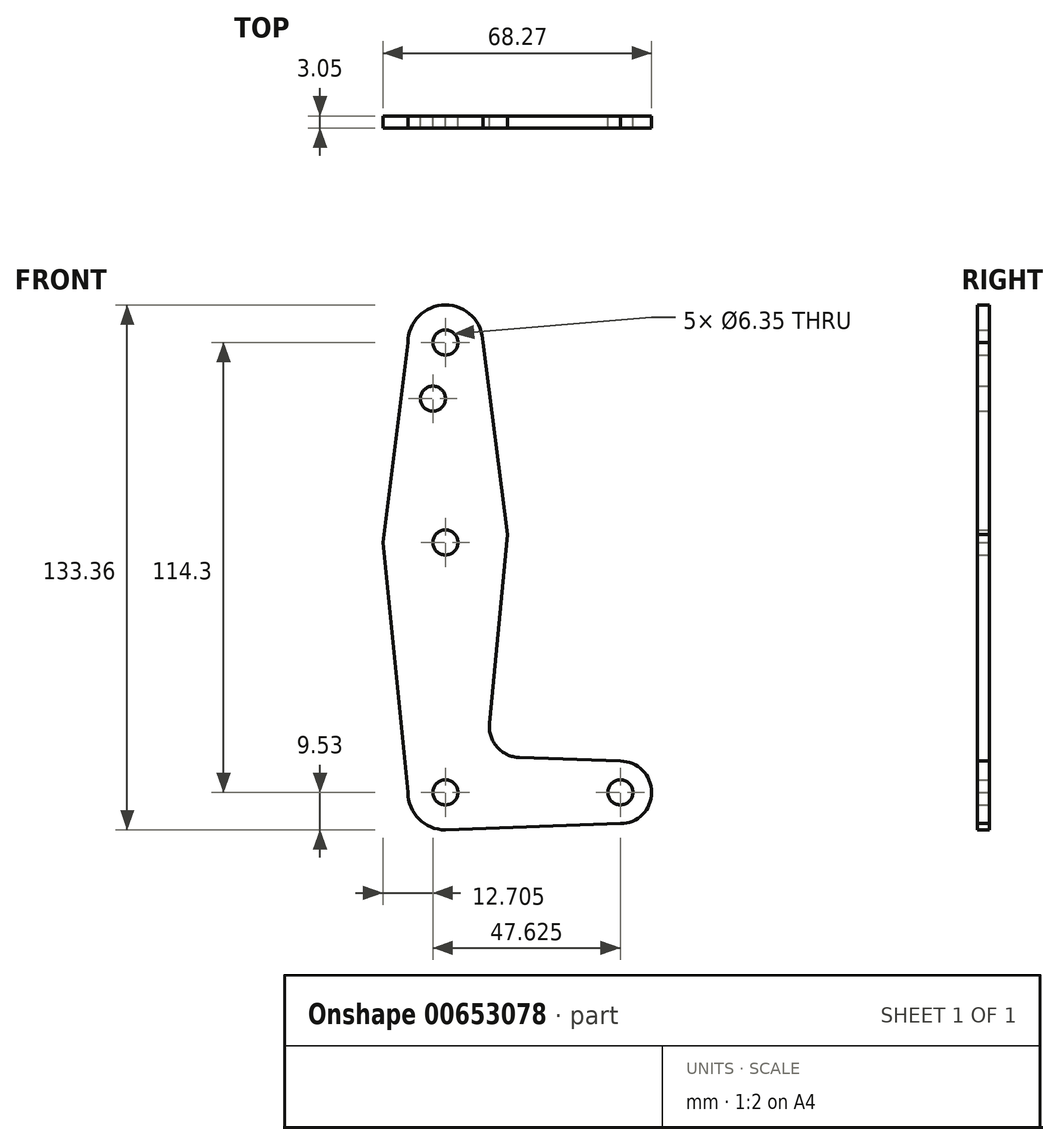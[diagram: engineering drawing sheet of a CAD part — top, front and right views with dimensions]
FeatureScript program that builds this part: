
annotation { "Feature Type Name" : "Feature", "Feature Type Description" : "" }
export const myFeature = defineFeature(function(context is Context, id is Id, definition is map)
    precondition{}
    {
        {
            var Q0;
            Q0=qCreatedBy(makeId("Front.planeOp"),FACE);
            var sketch = newSketch(context, id + "F0", { "sketchPlane" : qUnion([Q0])});
            skLineSegment(sketch, "E0", {"start": v(0, 0) * mm, "end": v(0, 114.3) * mm});
            skLineSegment(sketch, "E1", {"start": v(0, 0) * mm, "end": v(44.45, 0) * mm});
            skCircle(sketch, "E2", {"center": v(0, 114.3) * mm, "radius": 9.53 * mm});
            skCircle(sketch, "E3", {"center": v(0, 0) * mm, "radius": 9.53 * mm});
            skCircle(sketch, "E4", {"center": v(44.45, 0) * mm, "radius": 7.94 * mm});
            skCircle(sketch, "E5", {"center": v(0, 63.5) * mm, "radius": 15.88 * mm});
            skLineSegment(sketch, "E6", {"start": v(-9.52, 114.3) * mm, "end": v(-15.88, 63.5) * mm});
            skLineSegment(sketch, "E7", {"start": v(-15.87, 63.5) * mm, "end": v(-9.53, 0) * mm});
            skLineSegment(sketch, "E8", {"start": v(9.53, 114.3) * mm, "end": v(15.75, 65.5) * mm});
            skLineSegment(sketch, "E9", {"start": v(15.75, 65.5) * mm, "end": v(11.2, 17.55) * mm});
            skLineSegment(sketch, "E10", {"start": v(0, -9.52) * mm, "end": v(44.45, -7.94) * mm});
            skLineSegment(sketch, "E11", {"start": v(18.82, 8.85) * mm, "end": v(44.45, 7.94) * mm});
            skCircle(sketch, "E12", {"center": v(0, 114.3) * mm, "radius": 3.18 * mm});
            skCircle(sketch, "E13", {"center": v(0, 63.5) * mm, "radius": 3.18 * mm});
            skCircle(sketch, "E14", {"center": v(0, 0) * mm, "radius": 3.18 * mm});
            skCircle(sketch, "E15", {"center": v(44.45, 0) * mm, "radius": 3.18 * mm});
            skCircle(sketch, "E16", {"center": v(-3.18, 100.03) * mm, "radius": 3.18 * mm});
            skArc(sketch, "E17.filletArc", {"start": v(11.2, 17.55) * mm, "mid": v(13.13, 11.55) * mm, "end": v(18.82, 8.85) * mm});
            skSolve(sketch);
        }
        {
            var Q0;
            Q0=makeQuery(id+"F0.imprint","IMPRINT",FACE,{"disambiguationData":[TD([[makeQuery(id+"F0.imprint","IMPRINT",EDGE,{"derivedFrom":sQuery(id+"F0.wireOp",EDGE,"E12")}),-1.0]])]});
            var Q1;
            {var subQ0=sQuery(id+"F0.wireOp",EDGE,"E8");Q1=makeQuery(id+"F0.imprint","IMPRINT",FACE,{"disambiguationData":[TD([[makeQuery(id+"F0.imprint","IMPRINT",EDGE,{"derivedFrom":subQ0}),-1.0]])]});}
            var Q2;
            {var subQ8=sQuery(id+"F0.wireOp",EDGE,"E16");Q2=makeQuery(id+"F0.imprint","IMPRINT",FACE,{"disambiguationData":[TD([[makeQuery(id+"F0.imprint","IMPRINT",EDGE,{"derivedFrom":subQ8}),-1.0]])]});}
            var Q3;
            {var subQ1=sQuery(id+"F0.wireOp",EDGE,"E5");var subQ3=sQuery(id+"F0.wireOp",EDGE,"E0");var subQ4=makeQuery(id+"F0.imprint","INTERSECT",VERTEX,{"disambiguationData":[OD(0.0)],"derivedFrom":[subQ3,subQ1]});Q3=makeQuery(id+"F0.imprint","IMPRINT",FACE,{"disambiguationData":[TD([[makeQuery(id+"F0.imprint","IMPRINT",EDGE,{"disambiguationData":[TD([[subQ4,-1.0]])],"derivedFrom":subQ3}),1.0]])]});}
            var Q4;
            {var subQ1=sQuery(id+"F0.wireOp",EDGE,"E5");var subQ3=sQuery(id+"F0.wireOp",EDGE,"E0");var subQ4=makeQuery(id+"F0.imprint","INTERSECT",VERTEX,{"disambiguationData":[OD(0.0)],"derivedFrom":[subQ3,subQ1]});Q4=makeQuery(id+"F0.imprint","IMPRINT",FACE,{"disambiguationData":[TD([[makeQuery(id+"F0.imprint","IMPRINT",EDGE,{"disambiguationData":[TD([[subQ4,-1.0]])],"derivedFrom":subQ3}),-1.0]])]});}
            var Q5;
            {var subQ0=sQuery(id+"F0.wireOp",EDGE,"E11");Q5=makeQuery(id+"F0.imprint","IMPRINT",FACE,{"disambiguationData":[TD([[makeQuery(id+"F0.imprint","IMPRINT",EDGE,{"derivedFrom":subQ0}),-1.0]])]});}
            var Q6;
            {var subQ0=sQuery(id+"F0.wireOp",EDGE,"E3");var subQ1=sQuery(id+"F0.wireOp",EDGE,"E0");var subQ2=makeQuery(id+"F0.imprint","INTERSECT",VERTEX,{"derivedFrom":[subQ1,subQ0]});Q6=makeQuery(id+"F0.imprint","IMPRINT",FACE,{"disambiguationData":[TD([[makeQuery(id+"F0.imprint","IMPRINT",EDGE,{"disambiguationData":[TD([[subQ2,-1.0]])],"derivedFrom":subQ1}),1.0]])]});}
            var Q7;
            {var subQ0=sQuery(id+"F0.wireOp",EDGE,"E14");var subQ1=sQuery(id+"F0.wireOp",EDGE,"E0");var subQ2=makeQuery(id+"F0.imprint","INTERSECT",VERTEX,{"derivedFrom":[subQ1,subQ0]});Q7=makeQuery(id+"F0.imprint","IMPRINT",FACE,{"disambiguationData":[TD([[makeQuery(id+"F0.imprint","IMPRINT",EDGE,{"disambiguationData":[TD([[subQ2,-1.0]])],"derivedFrom":subQ1}),-1.0]])]});}
            var Q8;
            {var subQ0=sQuery(id+"F0.wireOp",EDGE,"E4");var subQ1=sQuery(id+"F0.wireOp",EDGE,"E1");var subQ2=makeQuery(id+"F0.imprint","INTERSECT",VERTEX,{"derivedFrom":[subQ1,subQ0]});Q8=makeQuery(id+"F0.imprint","IMPRINT",FACE,{"disambiguationData":[TD([[makeQuery(id+"F0.imprint","IMPRINT",EDGE,{"disambiguationData":[TD([[subQ2,1.0]])],"derivedFrom":subQ1}),-1.0]])]});}
            var Q9;
            {var subQ2=sQuery(id+"F0.wireOp",EDGE,"E0");var subQ4=sQuery(id+"F0.wireOp",EDGE,"E14");var subQ10=makeQuery(id+"F0.imprint","INTERSECT",VERTEX,{"derivedFrom":[subQ2,subQ4]});Q9=makeQuery(id+"F0.imprint","IMPRINT",FACE,{"disambiguationData":[TD([[makeQuery(id+"F0.imprint","IMPRINT",EDGE,{"disambiguationData":[TD([[subQ10,-1.0]])],"derivedFrom":subQ2}),1.0]])]});}
            var Q10;
            Q10=makeQuery(id+"F0.imprint","IMPRINT",FACE,{"disambiguationData":[TD([[makeQuery(id+"F0.imprint","IMPRINT",EDGE,{"derivedFrom":sQuery(id+"F0.wireOp",EDGE,"E15")}),-1.0]])]});
            extrude(context, id + "F1", {"entities" : qUnion([Q0, Q1, Q2, Q3, Q4, Q5, Q6, Q7, Q8, Q9, Q10]), "depth" : 3.05 * mm, "offsetDistance" : 25.4 * mm});
        }
    });
